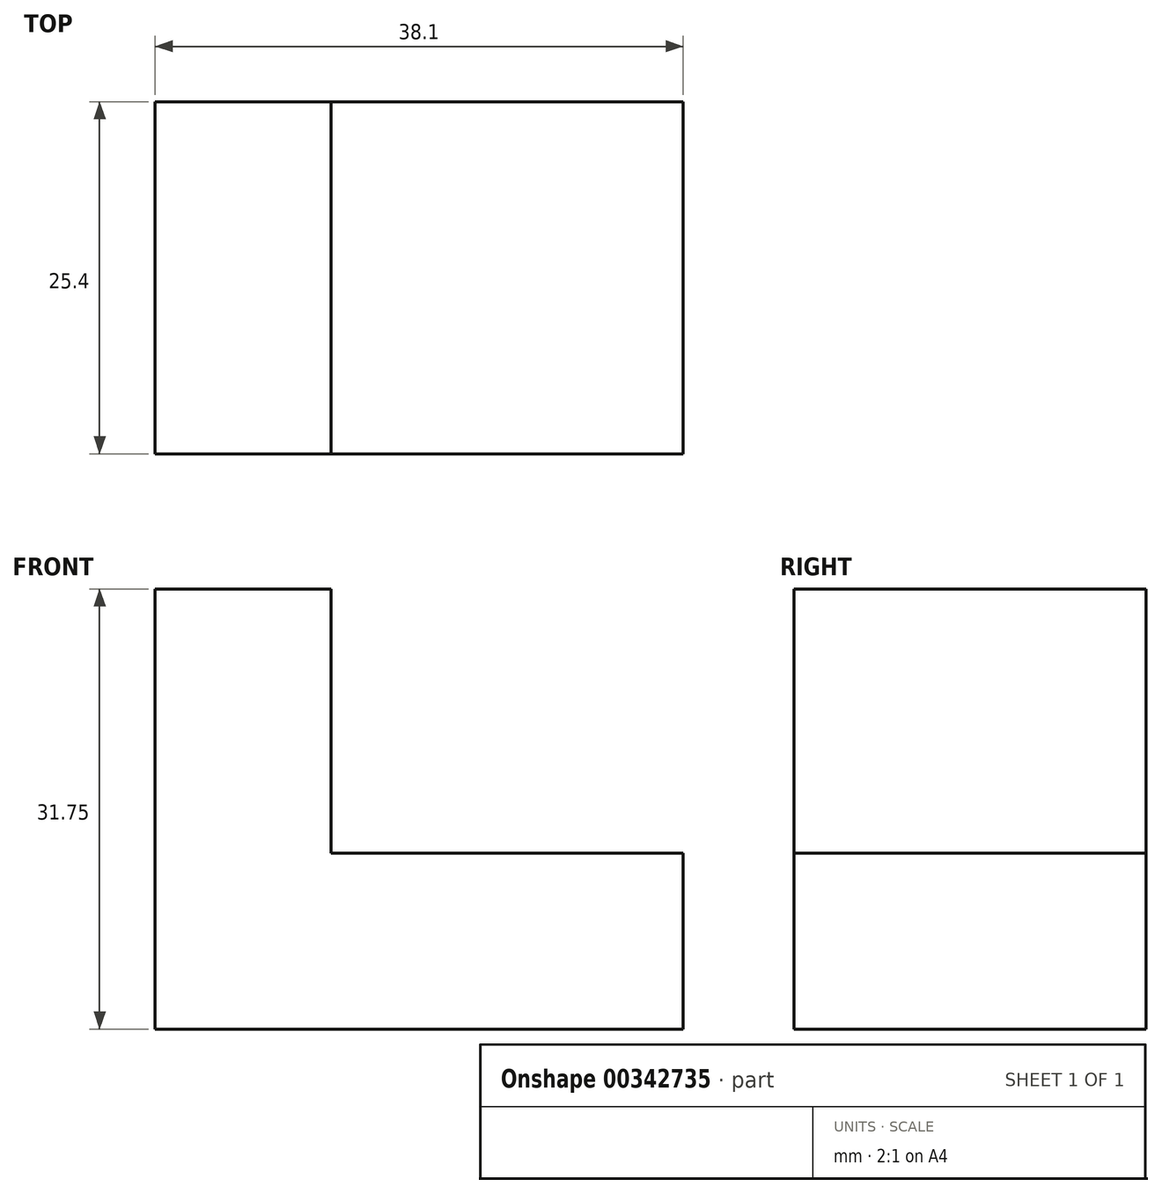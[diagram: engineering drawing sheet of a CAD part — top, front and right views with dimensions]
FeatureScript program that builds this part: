
annotation { "Feature Type Name" : "Feature", "Feature Type Description" : "" }
export const myFeature = defineFeature(function(context is Context, id is Id, definition is map)
    precondition{}
    {
        {
            var Q0;
            Q0=qCreatedBy(makeId("Front.planeOp"),FACE);
            var sketch = newSketch(context, id + "F0", { "sketchPlane" : qUnion([Q0])});
            skLineSegment(sketch, "E0", {"start": v(0, 0) * mm, "end": v(0, 31.75) * mm});
            skLineSegment(sketch, "E1", {"start": v(0, 31.75) * mm, "end": v(12.7, 31.75) * mm});
            skLineSegment(sketch, "E2", {"start": v(12.7, 31.75) * mm, "end": v(12.7, 12.7) * mm});
            skLineSegment(sketch, "E3", {"start": v(12.7, 12.7) * mm, "end": v(38.1, 12.7) * mm});
            skLineSegment(sketch, "E4", {"start": v(38.1, 12.7) * mm, "end": v(38.1, 0) * mm});
            skLineSegment(sketch, "E5", {"start": v(38.1, 0) * mm, "end": v(0, 0) * mm});
            skSolve(sketch);
        }
        {
            var Q0;
            Q0 = qSketchRegion(id + "F0", true);
            extrude(context, id + "F1", {"entities" : qUnion([Q0]), "oppositeDirection" : true, "depth" : 25.4 * mm});
        }
    });
